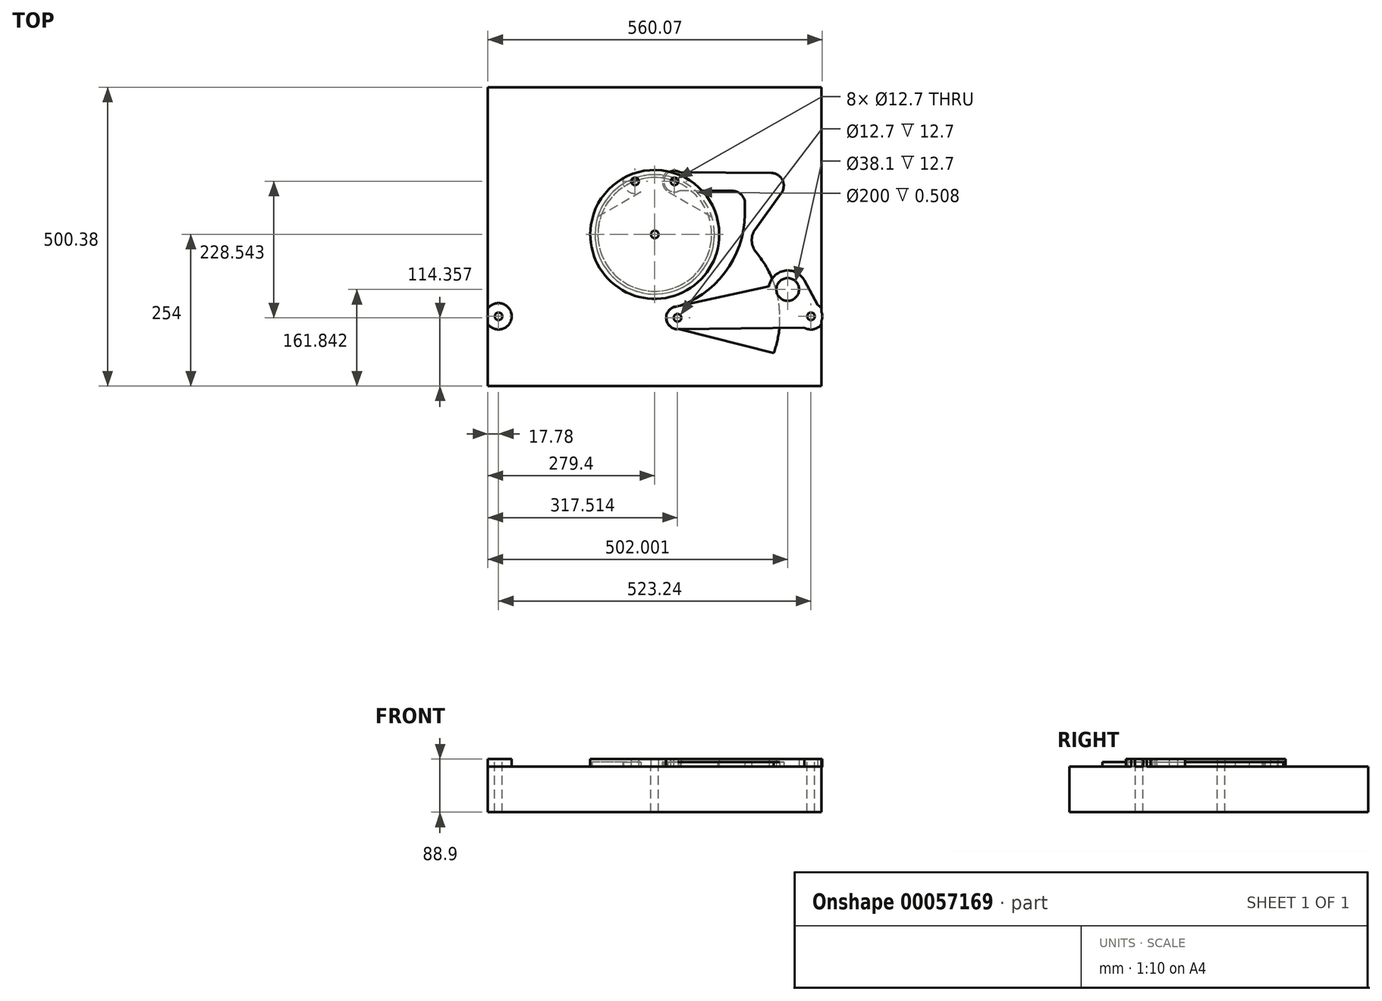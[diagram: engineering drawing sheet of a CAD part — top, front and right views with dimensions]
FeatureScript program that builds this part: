
annotation { "Feature Type Name" : "Feature", "Feature Type Description" : "" }
export const myFeature = defineFeature(function(context is Context, id is Id, definition is map)
    precondition{}
    {
        {
            var Q0;
            Q0=qCreatedBy(makeId("Top.planeOp"),FACE);
            var sketch = newSketch(context, id + "F0", { "sketchPlane" : qUnion([Q0])});
            skCircle(sketch, "E0", {"center": v(0, 0) * mm, "radius": 101.6 * mm});
            skCircle(sketch, "E1", {"center": v(0, 0) * mm, "radius": 203.2 * mm, "construction": true});
            skLineSegment(sketch, "E2.bottom", {"start": v(-279.4, 246.38) * mm, "end": v(279.4, 246.38) * mm});
            skLineSegment(sketch, "E2.top", {"start": v(-279.4, -254) * mm, "end": v(279.4, -254) * mm});
            skLineSegment(sketch, "E2.left", {"start": v(-279.4, 246.38) * mm, "end": v(-279.4, -254) * mm});
            skLineSegment(sketch, "E2.right", {"start": v(279.4, 246.38) * mm, "end": v(279.4, -254) * mm});
            skLineSegment(sketch, "E3", {"start": v(0, 0) * mm, "end": v(0, 176.93) * mm, "construction": true});
            skLineSegment(sketch, "E4", {"start": v(0, 0) * mm, "end": v(143.55, 0) * mm, "construction": true});
            skLineSegment(sketch, "E5", {"start": v(33.02, 88.9) * mm, "end": v(38.11, -139.64) * mm, "construction": true});
            skLineSegment(sketch, "E6", {"start": v(38.11, -139.64) * mm, "end": v(261.62, -137.16) * mm, "construction": true});
            skArc(sketch, "E7", {"start": v(61.42, -37.77) * mm, "mid": v(38.11, -139.64) * mm, "end": v(63.67, -240.97) * mm, "construction": true});
            skArc(sketch, "E8", {"start": v(135.13, 67.35) * mm, "mid": v(33, 88.9) * mm, "end": v(-68.07, 62.8) * mm, "construction": true});
            skLineSegment(sketch, "E9", {"start": v(261.62, -137.16) * mm, "end": v(63.67, -240.97) * mm, "construction": true});
            skLineSegment(sketch, "E10", {"start": v(261.62, -137.16) * mm, "end": v(61.42, -37.77) * mm, "construction": true});
            skLineSegment(sketch, "E11", {"start": v(38.11, -139.64) * mm, "end": v(-68.07, 62.8) * mm, "construction": true});
            skLineSegment(sketch, "E12", {"start": v(135.13, 67.35) * mm, "end": v(38.11, -139.64) * mm, "construction": true});
            skCircle(sketch, "E13", {"center": v(-93.98, 0) * mm, "radius": 101.6 * mm, "construction": true});
            skCircle(sketch, "E14", {"center": v(93.98, 0) * mm, "radius": 101.6 * mm, "construction": true});
            skCircle(sketch, "E15", {"center": v(0, 93.98) * mm, "radius": 101.6 * mm, "construction": true});
            skCircle(sketch, "E16", {"center": v(0, -93.98) * mm, "radius": 101.6 * mm, "construction": true});
            skCircle(sketch, "E17", {"center": v(0, 0) * mm, "radius": 93.98 * mm, "construction": true});
            skCircle(sketch, "E18", {"center": v(38.11, -139.64) * mm, "radius": 171.45 * mm});
            skLineSegment(sketch, "E19", {"start": v(38.11, -139.64) * mm, "end": v(204.4, -181.4) * mm});
            skLineSegment(sketch, "E20", {"start": v(38.11, -139.64) * mm, "end": v(166.12, -25.58) * mm});
            skLineSegment(sketch, "E21", {"start": v(38.11, -139.64) * mm, "end": v(222.6, -92.16) * mm});
            skCircle(sketch, "E22", {"center": v(222.6, -92.16) * mm, "radius": 19.05 * mm});
            skPoint(sketch, "E23", {"position": v(147.32, -213.36) * mm});
            skPoint(sketch, "E24", {"position": v(-81.28, 12.7) * mm});
            skLineSegment(sketch, "E25", {"start": v(-81.28, 12.7) * mm, "end": v(-76.19, -215.84) * mm, "construction": true});
            skLineSegment(sketch, "E26", {"start": v(147.32, -213.36) * mm, "end": v(-76.19, -215.84) * mm, "construction": true});
            skSolve(sketch);
        }
        {
            var Q0;
            Q0=qCreatedBy(makeId("Top.planeOp"),FACE);
            var sketch = newSketch(context, id + "F1", { "sketchPlane" : qUnion([Q0])});
            skLineSegment(sketch, "E27.bottom", {"start": v(279.4, 246.38) * mm, "end": v(-279.4, 246.38) * mm});
            skLineSegment(sketch, "E27.top", {"start": v(279.4, -254) * mm, "end": v(-279.4, -254) * mm});
            skLineSegment(sketch, "E27.left", {"start": v(279.4, 246.38) * mm, "end": v(279.4, -254) * mm});
            skLineSegment(sketch, "E27.right", {"start": v(-279.4, 246.38) * mm, "end": v(-279.4, -254) * mm});
            skCircle(sketch, "E28", {"center": v(261.62, -137.16) * mm, "radius": 6.35 * mm});
            skCircle(sketch, "E29", {"center": v(0, 0) * mm, "radius": 6.35 * mm});
            skLineSegment(sketch, "E30", {"start": v(0, 0) * mm, "end": v(0, 141.02) * mm, "construction": true});
            skCircle(sketch, "E31.MirrorC", {"center": v(-261.62, -137.16) * mm, "radius": 6.35 * mm});
            skSolve(sketch);
        }
        {
            var Q0;
            Q0=qCreatedBy(makeId("Top.planeOp"),FACE);
            var sketch = newSketch(context, id + "F2", { "sketchPlane" : qUnion([Q0])});
            skCircle(sketch, "E32", {"center": v(0, 0) * mm, "radius": 107.95 * mm});
            skCircle(sketch, "E33", {"center": v(33.02, 88.9) * mm, "radius": 6.35 * mm});
            skCircle(sketch, "E34", {"center": v(0, 0) * mm, "radius": 6.35 * mm});
            skLineSegment(sketch, "E35", {"start": v(0, 55.3) * mm, "end": v(0, 12.49) * mm, "construction": true});
            skCircle(sketch, "E36.MirrorC", {"center": v(-33.02, 88.9) * mm, "radius": 6.35 * mm});
            skSolve(sketch);
        }
        {
            var Q0;
            Q0=qCreatedBy(makeId("Top.planeOp"),FACE);
            var sketch = newSketch(context, id + "F3", { "sketchPlane" : qUnion([Q0])});
            skCircle(sketch, "E37", {"center": v(38.11, -139.64) * mm, "radius": 17.78 * mm});
            skCircle(sketch, "E38", {"center": v(33.02, 88.9) * mm, "radius": 17.78 * mm});
            skArc(sketch, "E39", {"start": v(199.17, -198.42) * mm, "mid": v(207.03, -110.27) * mm, "end": v(169.87, -29.94) * mm});
            skLineSegment(sketch, "E40", {"start": v(33.78, -156.89) * mm, "end": v(199.17, -198.42) * mm});
            skLineSegment(sketch, "E41", {"start": v(42.3, 104.07) * mm, "end": v(235.9, 102.56) * mm});
            skLineSegment(sketch, "E42", {"start": v(235.9, 102.56) * mm, "end": v(168.5, 8.92) * mm});
            skLineSegment(sketch, "E43", {"start": v(42.06, 73.59) * mm, "end": v(168.97, 72.6) * mm});
            skLineSegment(sketch, "E44", {"start": v(168.97, 72.6) * mm, "end": v(150.59, 47.06) * mm});
            skCircle(sketch, "E45", {"center": v(33.02, 88.9) * mm, "radius": 6.35 * mm});
            skCircle(sketch, "E46", {"center": v(38.11, -139.64) * mm, "radius": 6.35 * mm});
            skArc(sketch, "E47", {"start": v(33.04, -122.6) * mm, "mid": v(121.6, -58.4) * mm, "end": v(150.59, 47.06) * mm});
            skLineSegment(sketch, "E48", {"start": v(33.02, 88.9) * mm, "end": v(201.65, 87.59) * mm, "construction": true});
            skLineSegment(sketch, "E49", {"start": v(201.65, 87.59) * mm, "end": v(38.11, -139.64) * mm, "construction": true});
            skLineSegment(sketch, "E50", {"start": v(33.02, 88.9) * mm, "end": v(38.11, -139.64) * mm, "construction": true});
            skPoint(sketch, "E51.visualSharp", {"position": v(153.1, -12.47) * mm});
            skArc(sketch, "E51.filletArc", {"start": v(168.5, 8.92) * mm, "mid": v(162.54, -10.74) * mm, "end": v(169.87, -29.94) * mm});
            skSolve(sketch);
        }
        {
            var Q0;
            Q0=qCreatedBy(makeId("Top.planeOp"),FACE);
            var sketch = newSketch(context, id + "F4", { "sketchPlane" : qUnion([Q0])});
            skCircle(sketch, "E52", {"center": v(38.11, -139.64) * mm, "radius": 19.05 * mm});
            skCircle(sketch, "E53", {"center": v(222.6, -92.16) * mm, "radius": 31.75 * mm});
            skCircle(sketch, "E54", {"center": v(261.62, -137.16) * mm, "radius": 19.05 * mm});
            skLineSegment(sketch, "E55", {"start": v(38.33, -158.7) * mm, "end": v(261.83, -156.2) * mm});
            skLineSegment(sketch, "E56", {"start": v(250.47, -76.95) * mm, "end": v(278.34, -128.04) * mm});
            skLineSegment(sketch, "E57", {"start": v(191.28, -86.93) * mm, "end": v(34.08, -121.03) * mm});
            skCircle(sketch, "E58", {"center": v(38.11, -139.64) * mm, "radius": 6.35 * mm});
            skCircle(sketch, "E59", {"center": v(222.6, -92.16) * mm, "radius": 19.05 * mm});
            skCircle(sketch, "E60", {"center": v(261.62, -137.16) * mm, "radius": 6.35 * mm});
            skSolve(sketch);
        }
        {
            var Q0;
            Q0=makeQuery(id+"F1.imprint","IMPRINT",FACE,{"disambiguationData":[TD([[makeQuery(id+"F1.imprint","IMPRINT",EDGE,{"derivedFrom":sQuery(id+"F1.wireOp",EDGE,"E27.bottom")}),1.0]])]});
            extrude(context, id + "F5", {"entities" : qUnion([Q0]), "oppositeDirection" : true, "depth" : 76.2 * mm});
        }
        {
            var Q0;
            Q0=makeQuery(id+"F2.imprint","IMPRINT",FACE,{"disambiguationData":[TD([[makeQuery(id+"F2.imprint","IMPRINT",EDGE,{"derivedFrom":sQuery(id+"F2.wireOp",EDGE,"E32")}),1.0]])]});
            extrude(context, id + "F6", {"entities" : qUnion([Q0]), "depth" : 12.7 * mm});
        }
        {
            var Q0;
            Q0=makeQuery(id+"F2.imprint","IMPRINT",FACE,{"disambiguationData":[TD([[makeQuery(id+"F2.imprint","IMPRINT",EDGE,{"derivedFrom":sQuery(id+"F2.wireOp",EDGE,"E32")}),1.0]])]});
            var sketch = newSketch(context, id + "F7", { "sketchPlane" : qUnion([Q0])});
            skArc(sketch, "E61", {"start": v(21.67, 105.75) * mm, "mid": v(25.94, 69.85) * mm, "end": v(52.62, 94.26) * mm});
            skArc(sketch, "E62", {"start": v(105.32, 23.7) * mm, "mid": v(75.6, 77.06) * mm, "end": v(21.67, 105.75) * mm});
            skLineSegment(sketch, "E63", {"start": v(22.86, 71.3) * mm, "end": v(105.32, 23.7) * mm});
            skLineSegment(sketch, "E64", {"start": v(0, 8.7) * mm, "end": v(0, 56.69) * mm, "construction": true});
            skLineSegment(sketch, "E65.MirrorCS", {"start": v(-22.86, 71.3) * mm, "end": v(-105.32, 23.7) * mm});
            skArc(sketch, "E66.MirrorCS", {"start": v(-105.32, 23.7) * mm, "mid": v(-75.6, 77.06) * mm, "end": v(-21.67, 105.75) * mm});
            skArc(sketch, "E67.MirrorCS", {"start": v(-21.67, 105.75) * mm, "mid": v(-25.94, 69.85) * mm, "end": v(-52.62, 94.26) * mm});
            skSolve(sketch);
        }
        {
            var Q0;
            Q0=makeQuery(id+"F7.imprint","IMPRINT",FACE,{"disambiguationData":[TD([[makeQuery(id+"F7.imprint","IMPRINT",EDGE,{"derivedFrom":makeQuery(id+"F2.imprint","IMPRINT",EDGE,{"derivedFrom":sQuery(id+"F2.wireOp",EDGE,"E33")})}),-1.0]])]});
            var Q1;
            {var subQ0=sQuery(id+"F7.wireOp",EDGE,"E63");Q1=makeQuery(id+"F7.imprint","IMPRINT",FACE,{"disambiguationData":[TD([[makeQuery(id+"F7.imprint","IMPRINT",EDGE,{"derivedFrom":subQ0}),1.0]])]});}
            var Q2;
            {var subQ3=sQuery(id+"F7.wireOp",EDGE,"E65.MirrorCS");Q2=makeQuery(id+"F7.imprint","IMPRINT",FACE,{"disambiguationData":[TD([[makeQuery(id+"F7.imprint","IMPRINT",EDGE,{"derivedFrom":subQ3}),-1.0]])]});}
            var Q3;
            Q3=makeQuery(id+"F7.imprint","IMPRINT",FACE,{"disambiguationData":[TD([[makeQuery(id+"F7.imprint","IMPRINT",EDGE,{"derivedFrom":makeQuery(id+"F2.imprint","IMPRINT",EDGE,{"derivedFrom":sQuery(id+"F2.wireOp",EDGE,"E36.MirrorC")})}),1.0]])]});
            extrude(context, id + "F8", {"entities" : qUnion([Q0, Q1, Q2, Q3]), "operationType" : NewBodyOperationType.REMOVE, "depth" : 7.62 * mm});
        }
        {
            var Q0;
            Q0=makeQuery(id+"F3.imprint","IMPRINT",FACE,{"disambiguationData":[TD([[makeQuery(id+"F3.imprint","IMPRINT",EDGE,{"derivedFrom":sQuery(id+"F3.wireOp",EDGE,"E45")}),-1.0]])]});
            var Q1;
            {var subQ5=sQuery(id+"F3.wireOp",EDGE,"E41");Q1=makeQuery(id+"F3.imprint","IMPRINT",FACE,{"disambiguationData":[TD([[makeQuery(id+"F3.imprint","IMPRINT",EDGE,{"derivedFrom":subQ5}),-1.0]])]});}
            var Q2;
            {var subQ5=sQuery(id+"F3.wireOp",EDGE,"E40");Q2=makeQuery(id+"F3.imprint","IMPRINT",FACE,{"disambiguationData":[TD([[makeQuery(id+"F3.imprint","IMPRINT",EDGE,{"derivedFrom":subQ5}),1.0]])]});}
            var Q3;
            Q3=makeQuery(id+"F3.imprint","IMPRINT",FACE,{"disambiguationData":[TD([[makeQuery(id+"F3.imprint","IMPRINT",EDGE,{"derivedFrom":sQuery(id+"F3.wireOp",EDGE,"E46")}),-1.0]])]});
            extrude(context, id + "F9", {"entities" : qUnion([Q0, Q1, Q2, Q3]), "depth" : 7.62 * mm});
        }
        {
            var Q0;
            Q0=makeQuery(id+"F4.imprint","IMPRINT",FACE,{"disambiguationData":[TD([[makeQuery(id+"F4.imprint","IMPRINT",EDGE,{"derivedFrom":sQuery(id+"F4.wireOp",EDGE,"E58")}),-1.0]])]});
            var Q1;
            {var subQ2=sQuery(id+"F4.wireOp",EDGE,"E55");Q1=makeQuery(id+"F4.imprint","IMPRINT",FACE,{"disambiguationData":[TD([[makeQuery(id+"F4.imprint","IMPRINT",EDGE,{"derivedFrom":subQ2}),1.0]])]});}
            var Q2;
            Q2=makeQuery(id+"F4.imprint","IMPRINT",FACE,{"disambiguationData":[TD([[makeQuery(id+"F4.imprint","IMPRINT",EDGE,{"derivedFrom":sQuery(id+"F4.wireOp",EDGE,"E59")}),-1.0]])]});
            var Q3;
            Q3=makeQuery(id+"F4.imprint","IMPRINT",FACE,{"disambiguationData":[TD([[makeQuery(id+"F4.imprint","IMPRINT",EDGE,{"derivedFrom":sQuery(id+"F4.wireOp",EDGE,"E60")}),-1.0]])]});
            extrude(context, id + "F10", {"entities" : qUnion([Q0, Q1, Q2, Q3]), "depth" : 12.7 * mm});
        }
        {
            var Q0;
            Q0=makeQuery(id+"F5.opExtrude","CAP_FACE",FACE,{"disambiguationData":[OSD([sQuery(id+"F1.wireOp",EDGE,"E27.bottom"),sQuery(id+"F1.wireOp",EDGE,"E27.top"),sQuery(id+"F1.wireOp",EDGE,"E27.left"),sQuery(id+"F1.wireOp",EDGE,"E27.right"),sQuery(id+"F1.wireOp",EDGE,"E28")])],"isStart":true});
            var sketch = newSketch(context, id + "F11", { "sketchPlane" : qUnion([Q0])});
            skCircle(sketch, "E68", {"center": v(261.62, -137.16) * mm, "radius": 22.09 * mm});
            skLineSegment(sketch, "E69", {"start": v(279.4, -124.06) * mm, "end": v(279.4, -150.26) * mm});
            skLineSegment(sketch, "E70", {"start": v(0, 0) * mm, "end": v(0, 159.93) * mm, "construction": true});
            skCircle(sketch, "E71.MirrorC", {"center": v(-261.62, -137.16) * mm, "radius": 22.09 * mm});
            skLineSegment(sketch, "E72.MirrorCS", {"start": v(-279.4, -124.06) * mm, "end": v(-279.4, -150.26) * mm});
            skSolve(sketch);
        }
        {
            var Q0;
            {var subQ0=sQuery(id+"F11.wireOp",EDGE,"E69");Q0=makeQuery(id+"F11.imprint","IMPRINT",FACE,{"disambiguationData":[TD([[makeQuery(id+"F11.imprint","IMPRINT",EDGE,{"derivedFrom":subQ0}),-1.0]])]});}
            var Q1;
            {var subQ0=sQuery(id+"F11.wireOp",EDGE,"E72.MirrorCS");Q1=makeQuery(id+"F11.imprint","IMPRINT",FACE,{"disambiguationData":[TD([[makeQuery(id+"F11.imprint","IMPRINT",EDGE,{"derivedFrom":subQ0}),1.0]])]});}
            extrude(context, id + "F12", {"entities" : qUnion([Q0, Q1]), "operationType" : NewBodyOperationType.ADD, "depth" : 12.7 * mm});
        }
        {
            var Q0;
            Q0=qCreatedBy(makeId("Top.planeOp"),FACE);
            var sketch = newSketch(context, id + "F13", { "sketchPlane" : qUnion([Q0])});
            skCircle(sketch, "E73", {"center": v(0, 0) * mm, "radius": 100 * mm});
            skCircle(sketch, "E74", {"center": v(0, 0) * mm, "radius": 95.25 * mm});
            skSolve(sketch);
        }
        {
            var Q0;
            Q0=makeQuery(id+"F13.imprint","IMPRINT",FACE,{"disambiguationData":[TD([[makeQuery(id+"F13.imprint","IMPRINT",EDGE,{"derivedFrom":sQuery(id+"F13.wireOp",EDGE,"E73")}),1.0]])]});
            extrude(context, id + "F14", {"entities" : qUnion([Q0]), "operationType" : NewBodyOperationType.REMOVE, "oppositeDirection" : true, "depth" : 0.5 * mm});
        }
        {
            var Q0;
            Q0=makeQuery(id+"F9.opExtrude","SWEPT_EDGE",EDGE,{"disambiguationData":[OSD([sQuery(id+"F3.wireOp",EDGE,"E41"),sQuery(id+"F3.wireOp",EDGE,"E42")])]});
            var Q1;
            Q1=makeQuery(id+"F9.opExtrude","SWEPT_EDGE",EDGE,{"disambiguationData":[OSD([sQuery(id+"F3.wireOp",EDGE,"E43"),sQuery(id+"F3.wireOp",EDGE,"E44")])]});
            fillet(context, id + "F15", {"entities" : qUnion([Q0, Q1]), "radius" : 21.16 * mm, "tangentPropagation" : true, "allowEdgeOverflow" : false});
        }
    });
